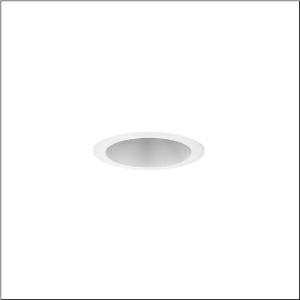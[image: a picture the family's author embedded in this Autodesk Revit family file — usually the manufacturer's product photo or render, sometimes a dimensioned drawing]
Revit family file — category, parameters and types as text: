
# Revit family: lunis_31-l_51dn15ee41b
name_source: partatom
category: Lighting Fixtures
units: mm (PartAtom-declared; Revit-internal decimal feet)

## family parameters
Cut with Voids When Loaded = No
Host = Face
Light Source = No
Part Type = Normal
Room Calculation Point = No
Round Connector Dimension = Use Diameter
Shared = No

## types (1)
- --- (1 x LED, 1750 lm, 12.2 W, 4000K)
    Apparent Load = 12 VA
    CIE Flux Codes = 93 98 100 100 100
    Color Rendering = 80
    Color Temperature = 4000K
    Default Elevation = 1800 mm
    Description = Lunis 31-L, downlight, light control with reflector, light emission: direct distribution, LED rated luminous flux: 1.750lm, light colour: 840, mains connection: 220..240V, AC/DC, 0/50..60Hz, housing, of aluminium, white, protection rating (complete): IP20, protection rating (on room side): IP54, insulation class (complete): insulation class II (safety insulation), certification: CE, ENEC, packaging unit: 1 piece
    Height = 0 mm  [stored 0 ft]
    Lamp = 1 x LED
    Lamp Light Flux = 1750 lm
    Lamp Power = 12.2 W
    Lamp count = 1
    Length = 188 mm  [stored 0.616798 ft]
    Luminous efficacy = 143 lm/W
    Manufacturer = Siteco
    ModVariant = No
    Model = 51DN15EE41B
    Mounting Place = Ceiling
    Mounting Type = Recessed
    Number of Poles = 1
    OnlyDefault = Yes
    Power Factor = 1
    Product Name = Lunis 31-L
    Product group = downlight
    ProductGroupID = 401
    Protection Class = Protection class II
    Protection Degree = IP 20
    RLX_Detail_Level = 1
    RLX_Emergency_Light_Flux = 0 lm
    RLX_Emergency_Type = 0
    RLX_Emergency_Type_DB = No
    RlxData = <blob elided: 22237 chars, md5=9771431a>
    Socket = socket
    Standby Power = 0 W
    System Light Flux = 1750 lm
    System Power = 12 W
    Type Comments = individual setting: luminous flux: 100 % | (OFF | ON) | 300 mA
    Type Image = l_1345911.jpg
    URL = http://relux.com
    VarID = @adj_031225
    Voltage = 0 V
    Weight = 0.00 kg
    Width = 0 mm  [stored 0 ft]

note: [stored X ft] marks values corroborated as IEEE doubles in the binary element streams (Revit-internal decimal feet)

## geometry (parser evidence)
native form markers: Blend x4, Sweep x10
no freeform markers — native parametric forms only
